# Revit family: 208_SHR-_-_
name_source: partatom
category: Air Terminals
units: mm (PartAtom-declared; Revit-internal decimal feet)

## family parameters
Always vertical = Yes
Cut with Voids When Loaded = No
Part Type = Normal
Room Calculation Point = Yes
Round Connector Dimension = Use Diameter
Shared = No
Work Plane-Based = No

## types (10) — shared parameters
C1 = 9 mm  [stored 0.0295276 ft]
C1__ve = -9 mm  [stored -0.0295276 ft]
CAT0 = Yes
CL_Location_5000 = 5000 mm  [stored 16.4042 ft]
Description = GRILLE FOR RECTANGULAR DUCT WITH DOUBLE BARS
L_ARR = 400 mm  [stored 1.31234 ft]
Manufacturer = Alnor
URL = http://www.ventilation-alnor.co.uk
W_ARR = 400 mm  [stored 1.31234 ft]
XRefLineVPlnId = 7453
YRefLineVPlnId = 7456
magiPartTypeId = 208
magiProductFamilyId = SHR-*-*
zero-valued in all types: CLBTZ, H_ARR

## per-type parameters (varying)
| type | B | B1 | BB | H | H1 | HH | magiProductId |
| SHR 200 100 | 200 mm | 88 mm | 113 mm | 100 mm | 38 mm | 63 mm | SHR-200-100 |
| SHR 500 300 | 500 mm | 238 mm | 263 mm | 300 mm | 138 mm | 163 mm | SHR-500-300 |
| SHR 400 300 | 400 mm | 188 mm | 213 mm | 300 mm | 138 mm | 163 mm | SHR-400-300 |
| SHR 400 200 | 400 mm | 188 mm | 213 mm | 200 mm | 88 mm | 113 mm | SHR-400-200 |
| SHR 300 200 | 300 mm | 138 mm | 163 mm | 200 mm | 88 mm | 113 mm | SHR-300-200 |
| SHR 300 150 | 300 mm | 138 mm | 163 mm | 150 mm | 63 mm | 88 mm | SHR-300-150 |
| SHR 300 100 | 300 mm | 138 mm | 163 mm | 100 mm | 38 mm | 63 mm | SHR-300-100 |
| SHR 250 200 | 250 mm | 113 mm | 138 mm | 200 mm | 88 mm | 113 mm | SHR-250-200 |
| SHR 200 200 | 200 mm | 88 mm | 113 mm | 200 mm | 88 mm | 113 mm | SHR-200-200 |
| SHR 200 150 | 200 mm | 88 mm | 113 mm | 150 mm | 63 mm | 88 mm | SHR-200-150 |

note: column(s) folded — value = type name in every type: MC Product Code

note: [stored X ft] marks values corroborated as IEEE doubles in the binary element streams (Revit-internal decimal feet)

## geometry (parser evidence)
native form markers: Blend x4, Sweep x1
no freeform markers — native parametric forms only
